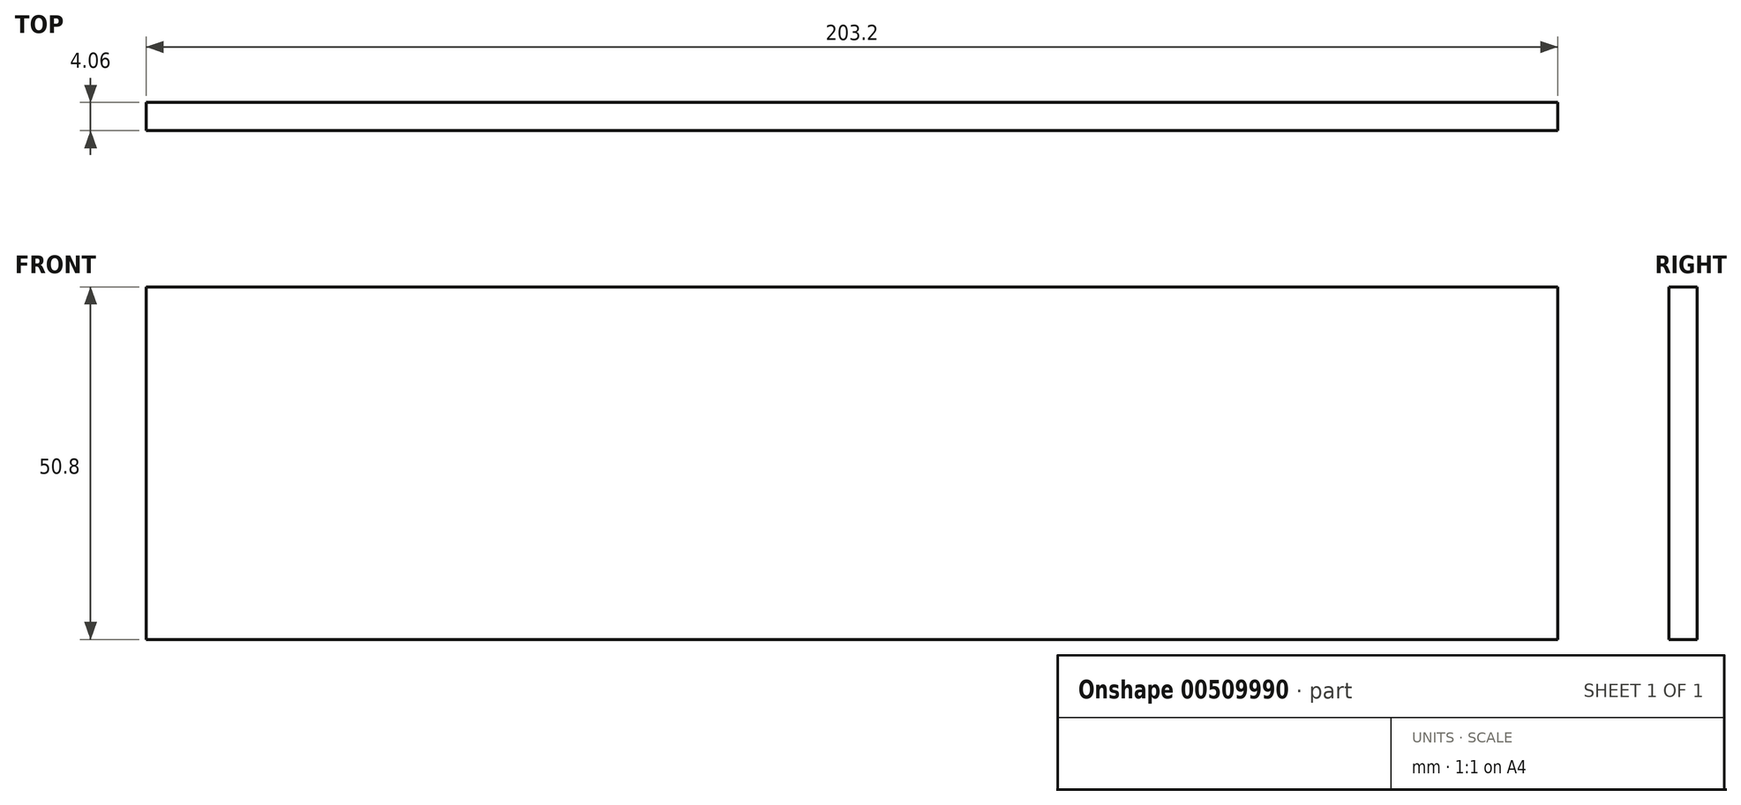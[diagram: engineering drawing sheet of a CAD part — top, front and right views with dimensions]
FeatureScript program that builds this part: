
annotation { "Feature Type Name" : "Feature", "Feature Type Description" : "" }
export const myFeature = defineFeature(function(context is Context, id is Id, definition is map)
    precondition{}
    {
        {
            var Q0;
            Q0=qCreatedBy(makeId("Front.planeOp"),FACE);
            var sketch = newSketch(context, id + "F0", { "sketchPlane" : qUnion([Q0])});
            skLineSegment(sketch, "E0.bottom", {"start": v(-95.7, 50.8) * mm, "end": v(107.5, 50.8) * mm});
            skLineSegment(sketch, "E0.top", {"start": v(-95.7, 0) * mm, "end": v(107.5, 0) * mm});
            skLineSegment(sketch, "E0.left", {"start": v(-95.7, 50.8) * mm, "end": v(-95.7, 0) * mm});
            skLineSegment(sketch, "E0.right", {"start": v(107.5, 50.8) * mm, "end": v(107.5, 0) * mm});
            skSolve(sketch);
        }
        {
            var Q0;
            Q0=makeQuery(id+"F0.imprint","IMPRINT",FACE,{"disambiguationData":[TD([[makeQuery(id+"F0.imprint","IMPRINT",EDGE,{"derivedFrom":sQuery(id+"F0.wireOp",EDGE,"E0.bottom")}),-1.0]])]});
            extrude(context, id + "F1", {"entities" : qUnion([Q0]), "depth" : 4.06 * mm, "offsetDistance" : 25.4 * mm});
        }
    });
